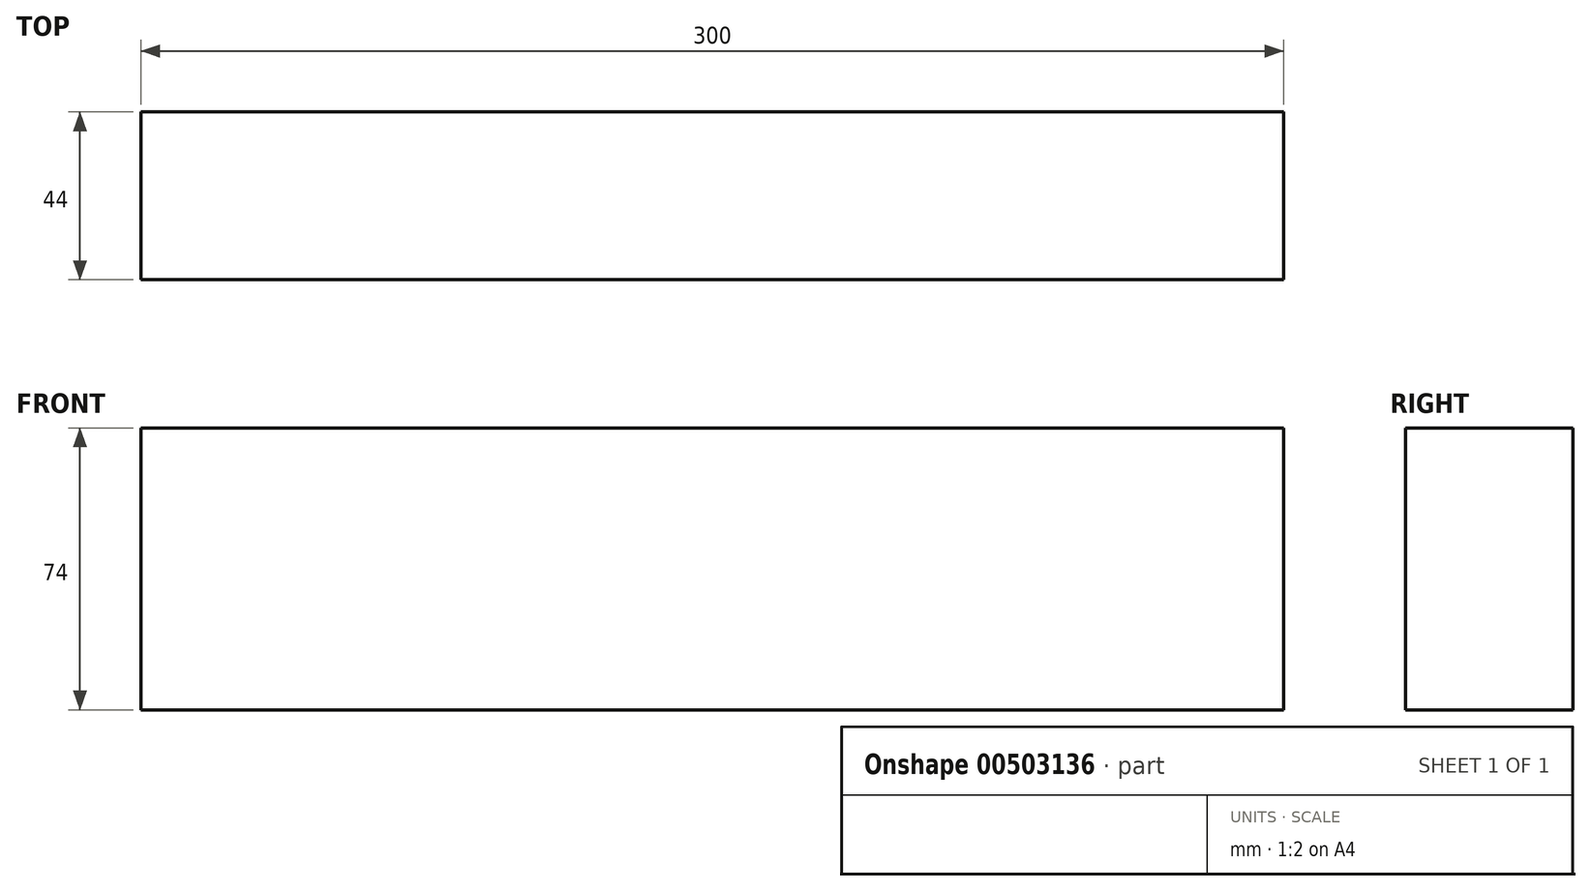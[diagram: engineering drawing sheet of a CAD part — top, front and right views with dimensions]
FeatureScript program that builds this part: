
annotation { "Feature Type Name" : "Feature", "Feature Type Description" : "" }
export const myFeature = defineFeature(function(context is Context, id is Id, definition is map)
    precondition{}
    {
        {
            var Q0;
            Q0=qCreatedBy(makeId("Front.planeOp"),FACE);
            var sketch = newSketch(context, id + "F0", { "sketchPlane" : qUnion([Q0])});
            skLineSegment(sketch, "E0.bottom", {"start": v(-410.5, 34.9) * mm, "end": v(-110.5, 34.9) * mm});
            skLineSegment(sketch, "E0.top", {"start": v(-410.5, -39.1) * mm, "end": v(-110.5, -39.1) * mm});
            skLineSegment(sketch, "E0.left", {"start": v(-410.5, 34.9) * mm, "end": v(-410.5, -39.1) * mm});
            skLineSegment(sketch, "E0.right", {"start": v(-110.5, 34.9) * mm, "end": v(-110.5, -39.1) * mm});
            skSolve(sketch);
        }
        {
            var Q0;
            Q0=makeQuery(id+"F0.imprint","IMPRINT",FACE,{"disambiguationData":[TD([[makeQuery(id+"F0.imprint","IMPRINT",EDGE,{"derivedFrom":sQuery(id+"F0.wireOp",EDGE,"E0.bottom")}),-1.0]])]});
            extrude(context, id + "F1", {"entities" : qUnion([Q0]), "depth" : 44 * mm, "offsetDistance" : 25 * mm});
        }
    });
